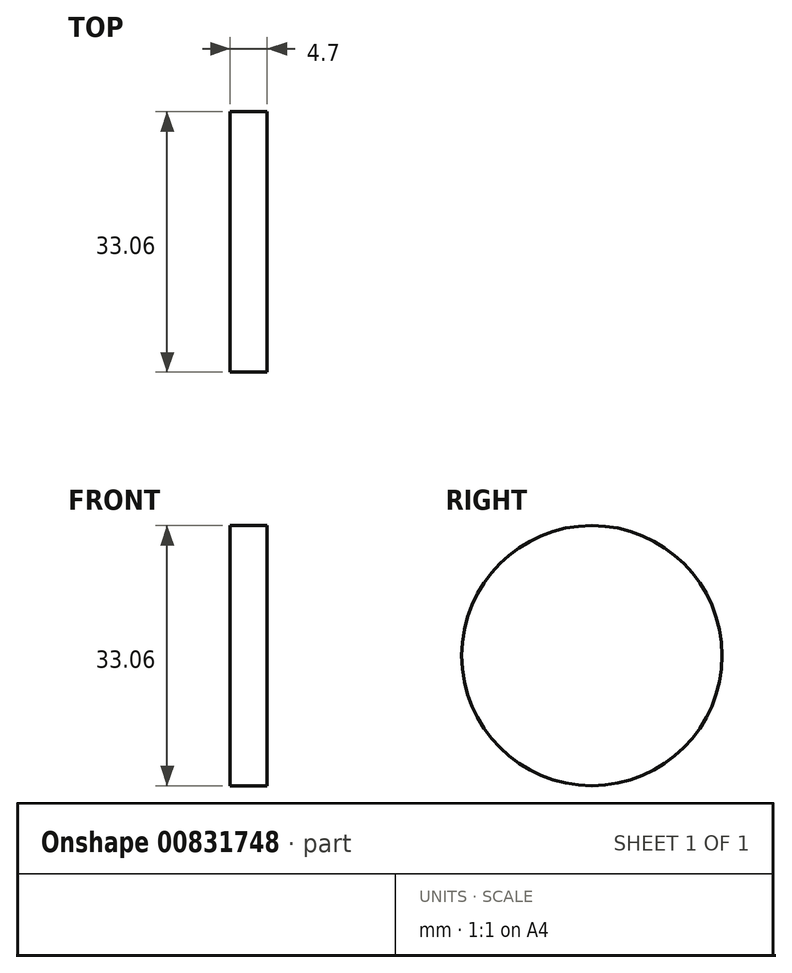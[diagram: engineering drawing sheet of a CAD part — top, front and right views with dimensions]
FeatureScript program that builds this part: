
annotation { "Feature Type Name" : "Feature", "Feature Type Description" : "" }
export const myFeature = defineFeature(function(context is Context, id is Id, definition is map)
    precondition{}
    {
        {
            var Q0;
            Q0=qCreatedBy(makeId("Right.planeOp"),FACE);
            var sketch = newSketch(context, id + "F0", { "sketchPlane" : qUnion([Q0])});
            skCircle(sketch, "E0", {"center": v(0.15, 0.45) * mm, "radius": 16.53 * mm});
            skSolve(sketch);
        }
        {
            var Q0;
            Q0 = qSketchRegion(id + "F0", true);
            var Q1;
            Q1=makeQuery(id+"F0.imprint","IMPRINT",FACE,{"disambiguationData":[TD([[makeQuery(id+"F0.imprint","IMPRINT",EDGE,{"derivedFrom":sQuery(id+"F0.wireOp",EDGE,"E0")}),1.0]])]});
            extrude(context, id + "F1", {"entities" : qUnion([Q0, Q1]), "depth" : 4.7 * mm, "offsetDistance" : 25 * mm});
        }
    });
